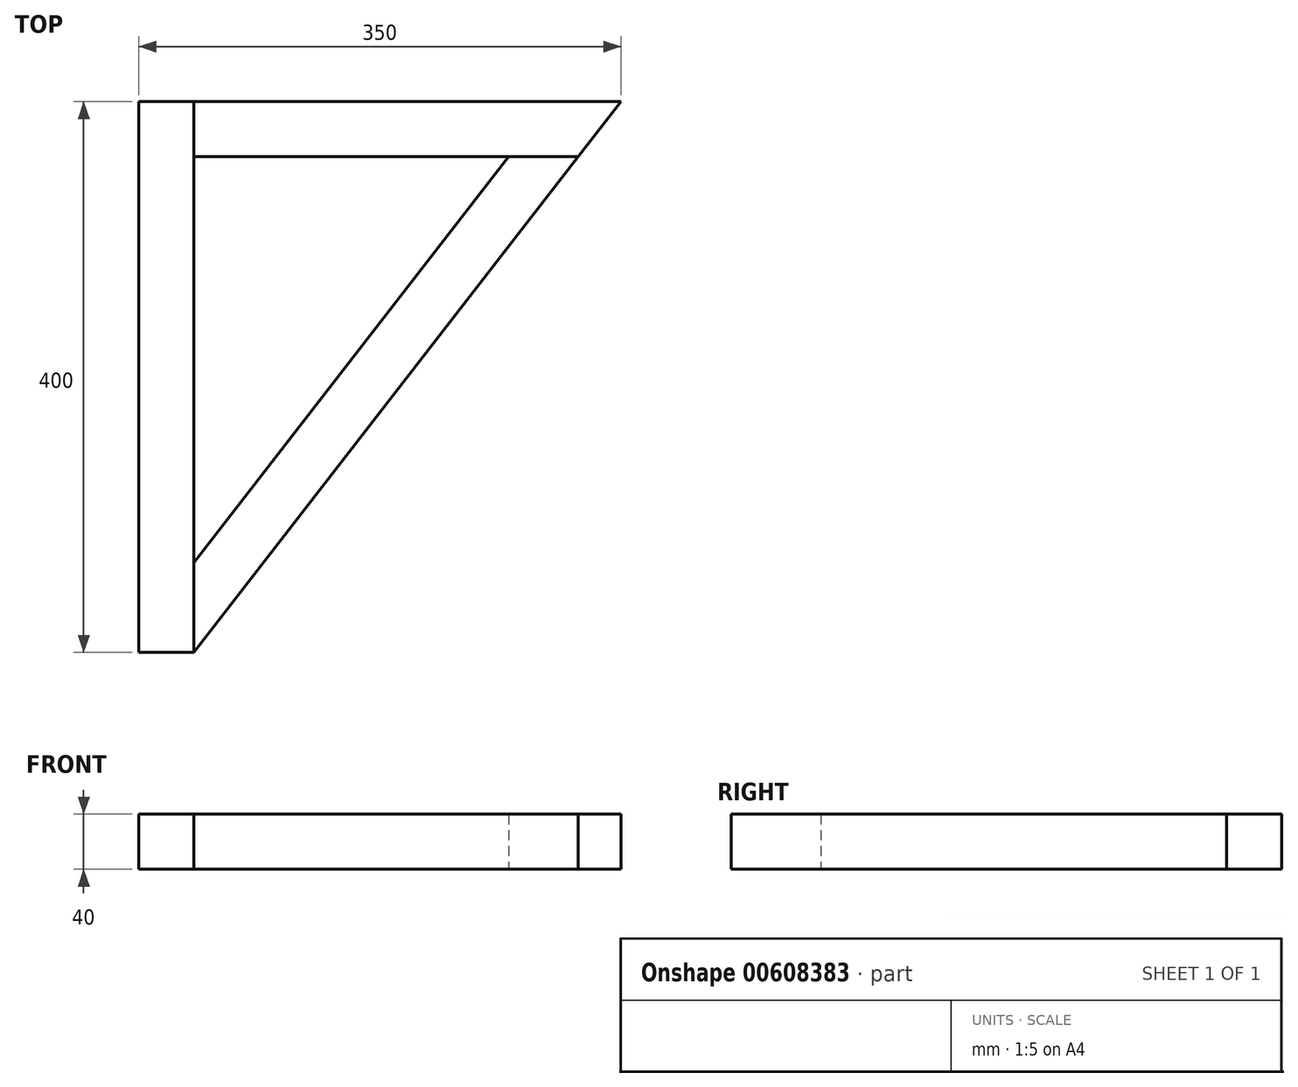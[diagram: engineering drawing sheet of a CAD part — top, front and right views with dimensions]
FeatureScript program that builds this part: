
annotation { "Feature Type Name" : "Feature", "Feature Type Description" : "" }
export const myFeature = defineFeature(function(context is Context, id is Id, definition is map)
    precondition{}
    {
        {
            var Q0;
            Q0=qCreatedBy(makeId("Top.planeOp"),FACE);
            var sketch = newSketch(context, id + "F0", { "sketchPlane" : qUnion([Q0])});
            skLineSegment(sketch, "E0", {"start": v(0, 0) * mm, "end": v(0, 400) * mm});
            skLineSegment(sketch, "E1", {"start": v(0, 400) * mm, "end": v(350, 400) * mm});
            skLineSegment(sketch, "E2", {"start": v(350, 400) * mm, "end": v(40, 0) * mm});
            skLineSegment(sketch, "E3", {"start": v(40, 0) * mm, "end": v(0, 0) * mm});
            skLineSegment(sketch, "E4", {"start": v(40, 0) * mm, "end": v(40, 400) * mm});
            skLineSegment(sketch, "E5", {"start": v(40, 360) * mm, "end": v(319, 360) * mm});
            skPoint(sketch, "E6.startSnap0", {"position": v(195, 200) * mm});
            skLineSegment(sketch, "E7", {"start": v(40, 65.3) * mm, "end": v(268.4, 360) * mm});
            skSolve(sketch);
        }
        {
            var Q0;
            {var subQ4=sQuery(id+"F0.wireOp",EDGE,"E1");var subQ6=sQuery(id+"F0.wireOp",EDGE,"E2");var subQ7=makeQuery(id+"F0.imprint","INTERSECT",VERTEX,{"derivedFrom":[subQ4,subQ6]});Q0=makeQuery(id+"F0.imprint","IMPRINT",FACE,{"disambiguationData":[TD([[makeQuery(id+"F0.imprint","IMPRINT",EDGE,{"disambiguationData":[TD([[subQ7,1.0]])],"derivedFrom":subQ4}),-1.0]])]});}
            extrude(context, id + "F1", {"entities" : qUnion([Q0]), "depth" : 40 * mm, "offsetDistance" : 25 * mm});
        }
        {
            var Q0;
            {var subQ5=sQuery(id+"F0.wireOp",EDGE,"E7");Q0=makeQuery(id+"F0.imprint","IMPRINT",FACE,{"disambiguationData":[TD([[makeQuery(id+"F0.imprint","IMPRINT",EDGE,{"derivedFrom":subQ5}),-1.0]])]});}
            extrude(context, id + "F2", {"entities" : qUnion([Q0]), "depth" : 40 * mm, "offsetDistance" : 25 * mm});
        }
        {
            var Q0;
            {var subQ4=sQuery(id+"F0.wireOp",EDGE,"E0");Q0=makeQuery(id+"F0.imprint","IMPRINT",FACE,{"disambiguationData":[TD([[makeQuery(id+"F0.imprint","IMPRINT",EDGE,{"derivedFrom":subQ4}),-1.0]])]});}
            extrude(context, id + "F3", {"entities" : qUnion([Q0]), "depth" : 40 * mm, "offsetDistance" : 25 * mm});
        }
    });
